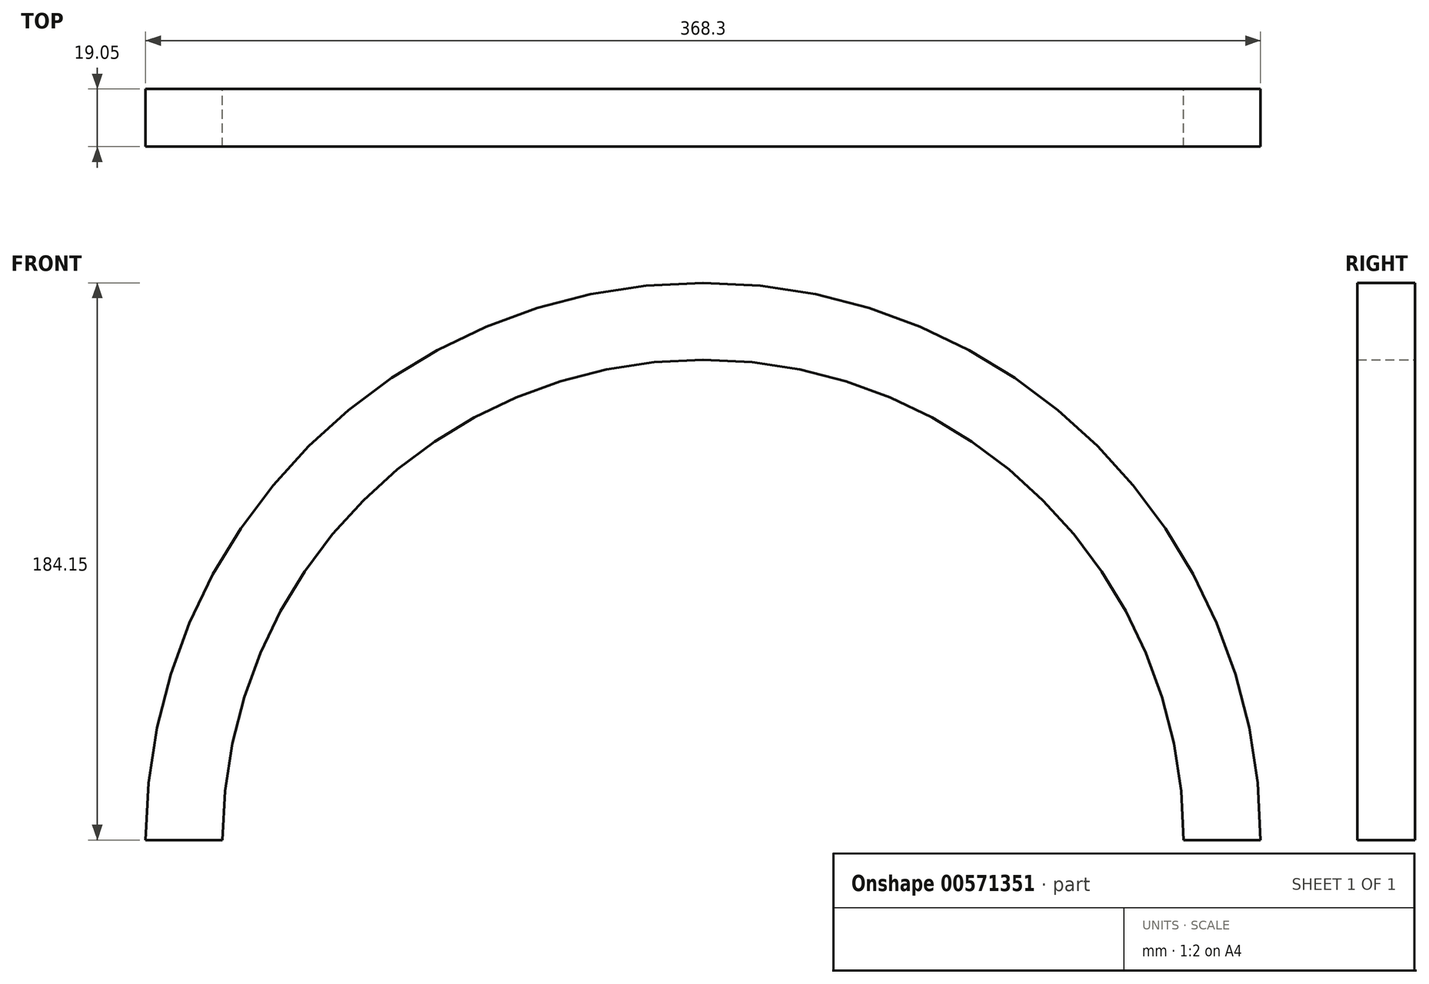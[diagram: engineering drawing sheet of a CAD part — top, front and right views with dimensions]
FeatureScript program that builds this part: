
annotation { "Feature Type Name" : "Feature", "Feature Type Description" : "" }
export const myFeature = defineFeature(function(context is Context, id is Id, definition is map)
    precondition{}
    {
        {
            var Q0;
            Q0=qCreatedBy(makeId("Front.planeOp"),FACE);
            var sketch = newSketch(context, id + "F0", { "sketchPlane" : qUnion([Q0])});
            skArc(sketch, "E0", {"start": v(158.75, 0) * mm, "mid": v(0, 158.75) * mm, "end": v(-158.75, 0) * mm});
            skArc(sketch, "E1", {"start": v(184.15, 0) * mm, "mid": v(0, 184.15) * mm, "end": v(-184.15, 0) * mm});
            skLineSegment(sketch, "E2", {"start": v(-184.15, 0) * mm, "end": v(-158.75, 0) * mm});
            skLineSegment(sketch, "E3.trimOffspring", {"start": v(158.75, 0) * mm, "end": v(184.15, 0) * mm});
            skSolve(sketch);
        }
        {
            var Q0;
            Q0 = qSketchRegion(id + "F0", true);
            extrude(context, id + "F1", {"entities" : qUnion([Q0]), "depth" : 19.05 * mm, "offsetDistance" : 25.4 * mm});
        }
    });
